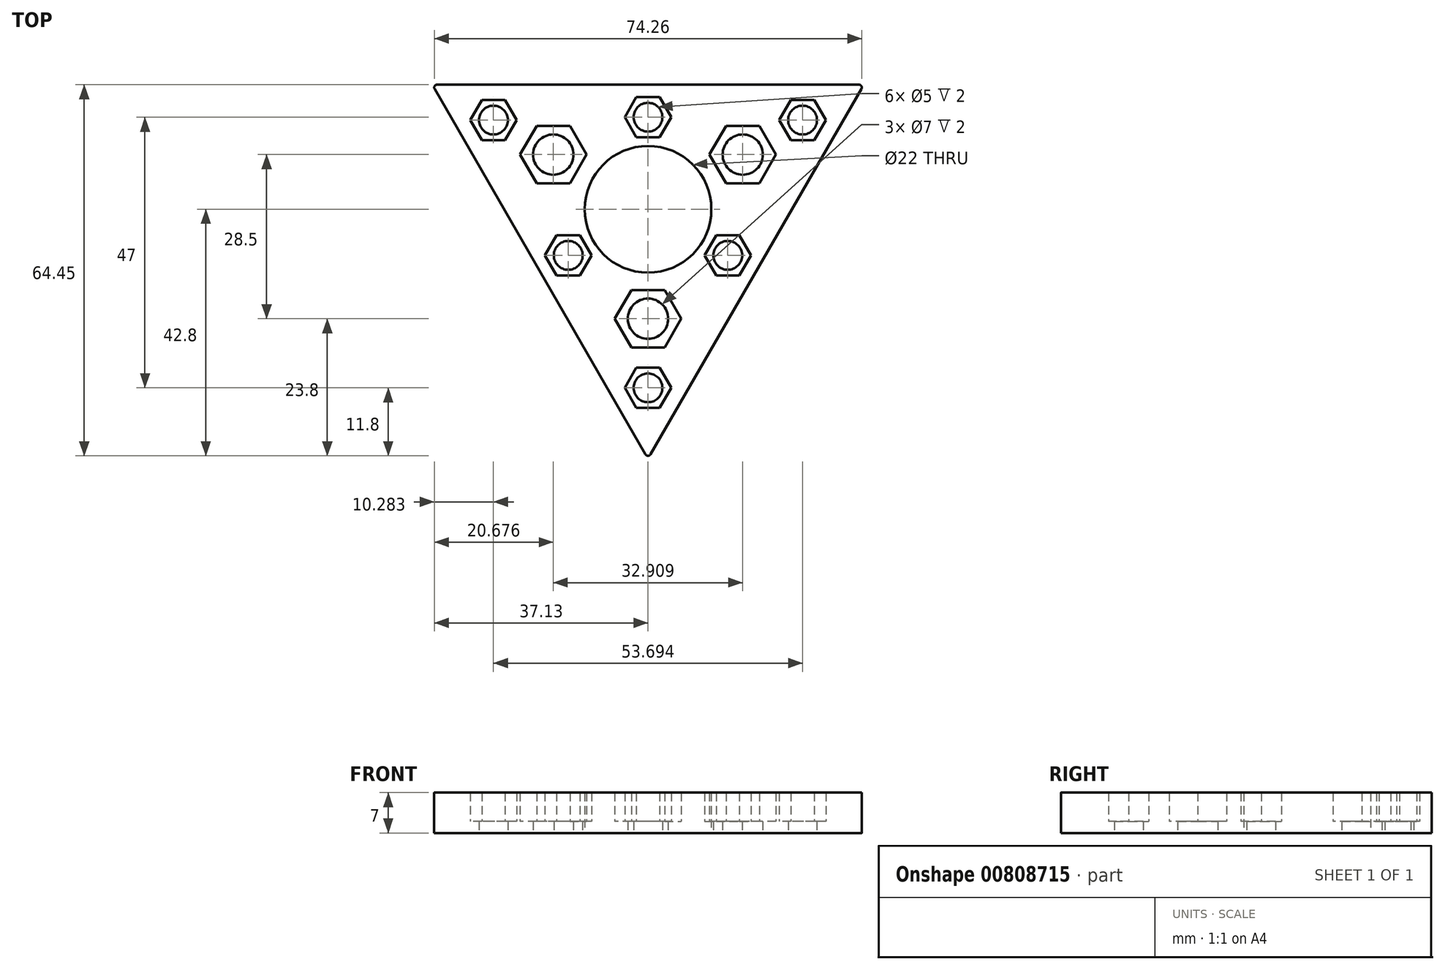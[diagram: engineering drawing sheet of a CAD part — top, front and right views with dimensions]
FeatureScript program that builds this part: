
annotation { "Feature Type Name" : "Feature", "Feature Type Description" : "" }
export const myFeature = defineFeature(function(context is Context, id is Id, definition is map)
    precondition{}
    {
        {
            var Q0;
            Q0=qCreatedBy(makeId("Top.planeOp"),FACE);
            var sketch = newSketch(context, id + "F0", { "sketchPlane" : qUnion([Q0])});
            skCircle(sketch, "E0", {"center": v(0, 0) * mm, "radius": 11 * mm});
            skCircle(sketch, "E1.cCircle", {"center": v(-26.85, 15.5) * mm, "radius": 3.5 * mm, "construction": true});
            skLineSegment(sketch, "E1.0", {"start": v(-24.83, 12) * mm, "end": v(-28.87, 12) * mm});
            skLineSegment(sketch, "E1.1", {"start": v(-28.87, 12) * mm, "end": v(-30.89, 15.5) * mm});
            skLineSegment(sketch, "E1.2", {"start": v(-30.89, 15.5) * mm, "end": v(-28.87, 19) * mm});
            skLineSegment(sketch, "E1.3", {"start": v(-28.87, 19) * mm, "end": v(-24.83, 19) * mm});
            skLineSegment(sketch, "E1.4", {"start": v(-24.83, 19) * mm, "end": v(-22.8, 15.5) * mm});
            skLineSegment(sketch, "E1.5", {"start": v(-22.8, 15.5) * mm, "end": v(-24.83, 12) * mm});
            skPoint(sketch, "E1.0.midPoint", {"position": v(-26.85, 12) * mm});
            skCircle(sketch, "E2.cCircle", {"center": v(26.85, 15.5) * mm, "radius": 3.5 * mm, "construction": true});
            skLineSegment(sketch, "E2.0", {"start": v(28.87, 12) * mm, "end": v(24.83, 12) * mm});
            skLineSegment(sketch, "E2.1", {"start": v(24.83, 12) * mm, "end": v(22.8, 15.5) * mm});
            skLineSegment(sketch, "E2.2", {"start": v(22.8, 15.5) * mm, "end": v(24.83, 19) * mm});
            skLineSegment(sketch, "E2.3", {"start": v(24.83, 19) * mm, "end": v(28.87, 19) * mm});
            skLineSegment(sketch, "E2.4", {"start": v(28.87, 19) * mm, "end": v(30.89, 15.5) * mm});
            skLineSegment(sketch, "E2.5", {"start": v(30.89, 15.5) * mm, "end": v(28.87, 12) * mm});
            skPoint(sketch, "E2.0.midPoint", {"position": v(26.85, 12) * mm});
            skCircle(sketch, "E3.cCircle", {"center": v(0, -31) * mm, "radius": 3.5 * mm, "construction": true});
            skLineSegment(sketch, "E3.0", {"start": v(2.02, -34.5) * mm, "end": v(-2.02, -34.5) * mm});
            skLineSegment(sketch, "E3.1", {"start": v(-2.02, -34.5) * mm, "end": v(-4.04, -31) * mm});
            skLineSegment(sketch, "E3.2", {"start": v(-4.04, -31) * mm, "end": v(-2.02, -27.5) * mm});
            skLineSegment(sketch, "E3.3", {"start": v(-2.02, -27.5) * mm, "end": v(2.02, -27.5) * mm});
            skLineSegment(sketch, "E3.4", {"start": v(2.02, -27.5) * mm, "end": v(4.04, -31) * mm});
            skLineSegment(sketch, "E3.5", {"start": v(4.04, -31) * mm, "end": v(2.02, -34.5) * mm});
            skPoint(sketch, "E3.0.midPoint", {"position": v(0, -34.5) * mm});
            skCircle(sketch, "E4.cCircle", {"center": v(-16.45, 9.5) * mm, "radius": 5 * mm, "construction": true});
            skLineSegment(sketch, "E4.0", {"start": v(-19.34, 4.5) * mm, "end": v(-22.23, 9.5) * mm});
            skLineSegment(sketch, "E4.1", {"start": v(-22.23, 9.5) * mm, "end": v(-19.34, 14.5) * mm});
            skLineSegment(sketch, "E4.2", {"start": v(-19.34, 14.5) * mm, "end": v(-13.57, 14.5) * mm});
            skLineSegment(sketch, "E4.3", {"start": v(-13.57, 14.5) * mm, "end": v(-10.68, 9.5) * mm});
            skLineSegment(sketch, "E4.4", {"start": v(-10.68, 9.5) * mm, "end": v(-13.57, 4.5) * mm});
            skLineSegment(sketch, "E4.5", {"start": v(-13.57, 4.5) * mm, "end": v(-19.34, 4.5) * mm});
            skPoint(sketch, "E4.0.midPoint", {"position": v(-20.78, 7) * mm});
            skCircle(sketch, "E5.cCircle", {"center": v(16.45, 9.5) * mm, "radius": 5 * mm, "construction": true});
            skLineSegment(sketch, "E5.0", {"start": v(19.34, 4.5) * mm, "end": v(13.57, 4.5) * mm});
            skLineSegment(sketch, "E5.1", {"start": v(13.57, 4.5) * mm, "end": v(10.68, 9.5) * mm});
            skLineSegment(sketch, "E5.2", {"start": v(10.68, 9.5) * mm, "end": v(13.57, 14.5) * mm});
            skLineSegment(sketch, "E5.3", {"start": v(13.57, 14.5) * mm, "end": v(19.34, 14.5) * mm});
            skLineSegment(sketch, "E5.4", {"start": v(19.34, 14.5) * mm, "end": v(22.23, 9.5) * mm});
            skLineSegment(sketch, "E5.5", {"start": v(22.23, 9.5) * mm, "end": v(19.34, 4.5) * mm});
            skPoint(sketch, "E5.0.midPoint", {"position": v(16.45, 4.5) * mm});
            skLineSegment(sketch, "E6", {"start": v(0, 0) * mm, "end": v(-37.4, 21.6) * mm, "construction": true});
            skLineSegment(sketch, "E7", {"start": v(0, 0) * mm, "end": v(37.1, 21.42) * mm, "construction": true});
            skCircle(sketch, "E8.cCircle", {"center": v(0, -19) * mm, "radius": 5 * mm, "construction": true});
            skLineSegment(sketch, "E8.0", {"start": v(5.77, -19) * mm, "end": v(2.89, -24) * mm});
            skLineSegment(sketch, "E8.1", {"start": v(2.89, -24) * mm, "end": v(-2.89, -24) * mm});
            skLineSegment(sketch, "E8.2", {"start": v(-2.89, -24) * mm, "end": v(-5.77, -19) * mm});
            skLineSegment(sketch, "E8.3", {"start": v(-5.77, -19) * mm, "end": v(-2.89, -14) * mm});
            skLineSegment(sketch, "E8.4", {"start": v(-2.89, -14) * mm, "end": v(2.89, -14) * mm});
            skLineSegment(sketch, "E8.5", {"start": v(2.89, -14) * mm, "end": v(5.77, -19) * mm});
            skPoint(sketch, "E8.0.midPoint", {"position": v(4.33, -21.5) * mm});
            skCircle(sketch, "E9.cCircle", {"center": v(-13.86, -8) * mm, "radius": 3.5 * mm, "construction": true});
            skLineSegment(sketch, "E9.0", {"start": v(-11.84, -11.5) * mm, "end": v(-15.88, -11.5) * mm});
            skLineSegment(sketch, "E9.1", {"start": v(-15.88, -11.5) * mm, "end": v(-17.9, -8) * mm});
            skLineSegment(sketch, "E9.2", {"start": v(-17.9, -8) * mm, "end": v(-15.88, -4.5) * mm});
            skLineSegment(sketch, "E9.3", {"start": v(-15.88, -4.5) * mm, "end": v(-11.84, -4.5) * mm});
            skLineSegment(sketch, "E9.4", {"start": v(-11.84, -4.5) * mm, "end": v(-9.81, -8) * mm});
            skLineSegment(sketch, "E9.5", {"start": v(-9.81, -8) * mm, "end": v(-11.84, -11.5) * mm});
            skPoint(sketch, "E9.0.midPoint", {"position": v(-13.86, -11.5) * mm});
            skCircle(sketch, "E10.cCircle", {"center": v(0, 16) * mm, "radius": 3.5 * mm, "construction": true});
            skLineSegment(sketch, "E10.0", {"start": v(2.02, 19.5) * mm, "end": v(4.04, 16) * mm});
            skLineSegment(sketch, "E10.1", {"start": v(4.04, 16) * mm, "end": v(2.02, 12.5) * mm});
            skLineSegment(sketch, "E10.2", {"start": v(2.02, 12.5) * mm, "end": v(-2.02, 12.5) * mm});
            skLineSegment(sketch, "E10.3", {"start": v(-2.02, 12.5) * mm, "end": v(-4.04, 16) * mm});
            skLineSegment(sketch, "E10.4", {"start": v(-4.04, 16) * mm, "end": v(-2.02, 19.5) * mm});
            skLineSegment(sketch, "E10.5", {"start": v(-2.02, 19.5) * mm, "end": v(2.02, 19.5) * mm});
            skPoint(sketch, "E10.0.midPoint", {"position": v(3.03, 17.75) * mm});
            skCircle(sketch, "E11.cCircle", {"center": v(13.86, -8) * mm, "radius": 3.5 * mm, "construction": true});
            skLineSegment(sketch, "E11.0", {"start": v(11.84, -4.5) * mm, "end": v(15.88, -4.5) * mm});
            skLineSegment(sketch, "E11.1", {"start": v(15.88, -4.5) * mm, "end": v(17.9, -8) * mm});
            skLineSegment(sketch, "E11.2", {"start": v(17.9, -8) * mm, "end": v(15.88, -11.5) * mm});
            skLineSegment(sketch, "E11.3", {"start": v(15.88, -11.5) * mm, "end": v(11.84, -11.5) * mm});
            skLineSegment(sketch, "E11.4", {"start": v(11.84, -11.5) * mm, "end": v(9.81, -8) * mm});
            skLineSegment(sketch, "E11.5", {"start": v(9.81, -8) * mm, "end": v(11.84, -4.5) * mm});
            skPoint(sketch, "E11.0.midPoint", {"position": v(13.86, -4.5) * mm});
            skLineSegment(sketch, "E12", {"start": v(0, 0) * mm, "end": v(23.11, -13.34) * mm, "construction": true});
            skLineSegment(sketch, "E13", {"start": v(0, 0) * mm, "end": v(-25.4, -14.67) * mm, "construction": true});
            skCircle(sketch, "E14.cCircle", {"center": v(0, 0) * mm, "radius": 21.65 * mm, "construction": true});
            skLineSegment(sketch, "E14.0", {"start": v(37.5, 21.65) * mm, "end": v(0, -43.3) * mm});
            skLineSegment(sketch, "E14.1", {"start": v(0, -43.3) * mm, "end": v(-37.5, 21.65) * mm});
            skLineSegment(sketch, "E14.2", {"start": v(-37.5, 21.65) * mm, "end": v(37.5, 21.65) * mm});
            skPoint(sketch, "E14.0.midPoint", {"position": v(18.75, -10.83) * mm});
            skCircle(sketch, "E15", {"center": v(-16.45, 9.5) * mm, "radius": 3.5 * mm});
            skCircle(sketch, "E16", {"center": v(16.45, 9.5) * mm, "radius": 3.5 * mm});
            skCircle(sketch, "E17", {"center": v(0, -19) * mm, "radius": 3.5 * mm});
            skCircle(sketch, "E18", {"center": v(0, -31) * mm, "radius": 2.5 * mm});
            skCircle(sketch, "E19", {"center": v(13.86, -8) * mm, "radius": 2.5 * mm});
            skCircle(sketch, "E20", {"center": v(26.85, 15.5) * mm, "radius": 2.5 * mm});
            skCircle(sketch, "E21", {"center": v(0, 16) * mm, "radius": 2.5 * mm});
            skCircle(sketch, "E22", {"center": v(-26.85, 15.5) * mm, "radius": 2.5 * mm});
            skCircle(sketch, "E23", {"center": v(-13.86, -8) * mm, "radius": 2.5 * mm});
            skSolve(sketch);
        }
        {
            var Q0;
            Q0=makeQuery(id+"F0.imprint","IMPRINT",FACE,{"disambiguationData":[TD([[makeQuery(id+"F0.imprint","IMPRINT",EDGE,{"derivedFrom":sQuery(id+"F0.wireOp",EDGE,"E0")}),-1.0]])]});
            extrude(context, id + "F1", {"entities" : qUnion([Q0]), "depth" : 7 * mm, "offsetDistance" : 25 * mm});
        }
        {
            var Q0;
            Q0=makeQuery(id+"F1.opExtrude","SWEPT_EDGE",EDGE,{"disambiguationData":[OSD([sQuery(id+"F0.wireOp",EDGE,"E14.0"),sQuery(id+"F0.wireOp",EDGE,"E14.1")])]});
            var Q1;
            Q1=makeQuery(id+"F1.opExtrude","SWEPT_EDGE",EDGE,{"disambiguationData":[OSD([sQuery(id+"F0.wireOp",EDGE,"E14.1"),sQuery(id+"F0.wireOp",EDGE,"E14.2")])]});
            var Q2;
            Q2=makeQuery(id+"F1.opExtrude","SWEPT_EDGE",EDGE,{"disambiguationData":[OSD([sQuery(id+"F0.wireOp",EDGE,"E14.0"),sQuery(id+"F0.wireOp",EDGE,"E14.2")])]});
            fillet(context, id + "F2", {"entities" : qUnion([Q0, Q1, Q2]), "radius" : 0.5 * mm, "tangentPropagation" : true, "allowEdgeOverflow" : false});
        }
        {
            var Q0;
            Q0=makeQuery(id+"F0.imprint","IMPRINT",FACE,{"disambiguationData":[TD([[makeQuery(id+"F0.imprint","IMPRINT",EDGE,{"derivedFrom":sQuery(id+"F0.wireOp",EDGE,"E10.0")}),-1.0]])]});
            var Q1;
            Q1=makeQuery(id+"F0.imprint","IMPRINT",FACE,{"disambiguationData":[TD([[makeQuery(id+"F0.imprint","IMPRINT",EDGE,{"derivedFrom":sQuery(id+"F0.wireOp",EDGE,"E4.0")}),-1.0]])]});
            var Q2;
            Q2=makeQuery(id+"F0.imprint","IMPRINT",FACE,{"disambiguationData":[TD([[makeQuery(id+"F0.imprint","IMPRINT",EDGE,{"derivedFrom":sQuery(id+"F0.wireOp",EDGE,"E9.0")}),-1.0]])]});
            var Q3;
            Q3=makeQuery(id+"F0.imprint","IMPRINT",FACE,{"disambiguationData":[TD([[makeQuery(id+"F0.imprint","IMPRINT",EDGE,{"derivedFrom":sQuery(id+"F0.wireOp",EDGE,"E1.0")}),-1.0]])]});
            var Q4;
            Q4=makeQuery(id+"F0.imprint","IMPRINT",FACE,{"disambiguationData":[TD([[makeQuery(id+"F0.imprint","IMPRINT",EDGE,{"derivedFrom":sQuery(id+"F0.wireOp",EDGE,"E8.0")}),-1.0]])]});
            var Q5;
            Q5=makeQuery(id+"F0.imprint","IMPRINT",FACE,{"disambiguationData":[TD([[makeQuery(id+"F0.imprint","IMPRINT",EDGE,{"derivedFrom":sQuery(id+"F0.wireOp",EDGE,"E3.0")}),-1.0]])]});
            var Q6;
            Q6=makeQuery(id+"F0.imprint","IMPRINT",FACE,{"disambiguationData":[TD([[makeQuery(id+"F0.imprint","IMPRINT",EDGE,{"derivedFrom":sQuery(id+"F0.wireOp",EDGE,"E11.0")}),-1.0]])]});
            var Q7;
            Q7=makeQuery(id+"F0.imprint","IMPRINT",FACE,{"disambiguationData":[TD([[makeQuery(id+"F0.imprint","IMPRINT",EDGE,{"derivedFrom":sQuery(id+"F0.wireOp",EDGE,"E5.0")}),-1.0]])]});
            var Q8;
            Q8=makeQuery(id+"F0.imprint","IMPRINT",FACE,{"disambiguationData":[TD([[makeQuery(id+"F0.imprint","IMPRINT",EDGE,{"derivedFrom":sQuery(id+"F0.wireOp",EDGE,"E2.0")}),-1.0]])]});
            extrude(context, id + "F3", {"entities" : qUnion([Q0, Q1, Q2, Q3, Q4, Q5, Q6, Q7, Q8]), "operationType" : NewBodyOperationType.ADD, "depth" : 2 * mm, "offsetDistance" : 25 * mm});
        }
    });
